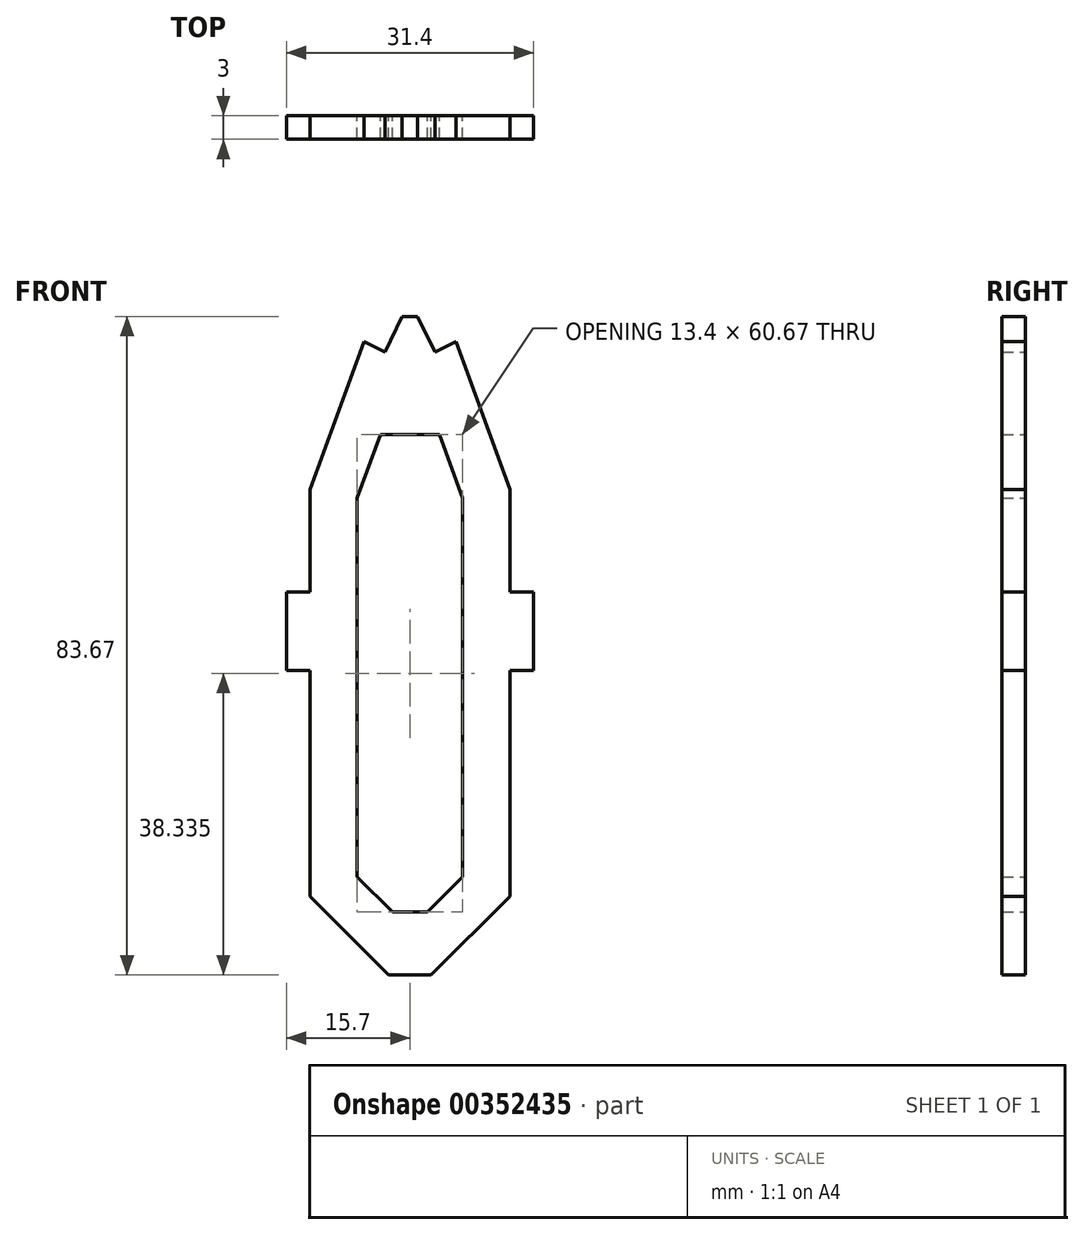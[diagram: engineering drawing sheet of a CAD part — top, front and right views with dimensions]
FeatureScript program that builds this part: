
annotation { "Feature Type Name" : "Feature", "Feature Type Description" : "" }
export const myFeature = defineFeature(function(context is Context, id is Id, definition is map)
    precondition{}
    {
        {
            var Q0;
            Q0=qCreatedBy(makeId("Front.planeOp"),FACE);
            var sketch = newSketch(context, id + "F0", { "sketchPlane" : qUnion([Q0])});
            skLineSegment(sketch, "E0.MirrorCS", {"start": v(5.86, 36.8) * mm, "end": v(3.16, 35.5) * mm});
            skLineSegment(sketch, "E1.MirrorCS", {"start": v(3.16, 35.5) * mm, "end": v(0.99, 40) * mm});
            skLineSegment(sketch, "E2.MirrorCS", {"start": v(12.7, 18) * mm, "end": v(5.86, 36.8) * mm});
            skLineSegment(sketch, "E3.MirrorCS", {"start": v(12.7, -33.67) * mm, "end": v(12.7, -5) * mm});
            skLineSegment(sketch, "E4.bottom", {"start": v(15.7, 5) * mm, "end": v(12.7, 5) * mm});
            skLineSegment(sketch, "E4.top", {"start": v(15.7, -5) * mm, "end": v(12.7, -5) * mm});
            skLineSegment(sketch, "E4.left", {"start": v(15.7, 5) * mm, "end": v(15.7, -5) * mm});
            skLineSegment(sketch, "E5.trimOffspring", {"start": v(12.7, 5) * mm, "end": v(12.7, 18) * mm});
            skLineSegment(sketch, "E6.MirrorCS", {"start": v(-15.7, 5) * mm, "end": v(-12.7, 5) * mm});
            skLineSegment(sketch, "E7.MirrorCS", {"start": v(-15.7, 5) * mm, "end": v(-15.7, -5) * mm});
            skLineSegment(sketch, "E8.MirrorCS", {"start": v(-15.7, -5) * mm, "end": v(-12.7, -5) * mm});
            skLineSegment(sketch, "E9", {"start": v(2.7, -43.67) * mm, "end": v(12.7, -33.67) * mm});
            skLineSegment(sketch, "E10.MirrorCS", {"start": v(-2.7, -43.67) * mm, "end": v(-12.7, -33.67) * mm});
            skLineSegment(sketch, "E11", {"start": v(2.7, -43.67) * mm, "end": v(0, -43.67) * mm});
            skLineSegment(sketch, "E12.MirrorCS", {"start": v(-2.7, -43.67) * mm, "end": v(0, -43.67) * mm});
            skLineSegment(sketch, "E13.MirrorCS", {"start": v(-12.7, -33.67) * mm, "end": v(-12.7, -5) * mm});
            skLineSegment(sketch, "E14", {"start": v(0.99, 40) * mm, "end": v(0, 40) * mm});
            skLineSegment(sketch, "E15.MirrorCS", {"start": v(-0.99, 40) * mm, "end": v(0, 40) * mm});
            skLineSegment(sketch, "E16.MirrorCS", {"start": v(-3.16, 35.5) * mm, "end": v(-0.99, 40) * mm});
            skLineSegment(sketch, "E17.MirrorCS", {"start": v(-5.86, 36.8) * mm, "end": v(-3.16, 35.5) * mm});
            skLineSegment(sketch, "E18.MirrorCS", {"start": v(-12.7, 18) * mm, "end": v(-5.86, 36.8) * mm});
            skLineSegment(sketch, "E19.MirrorCS", {"start": v(-12.7, 5) * mm, "end": v(-12.7, 18) * mm});
            skLineSegment(sketch, "E20", {"start": v(-12.7, 5) * mm, "end": v(-12.7, -5) * mm, "construction": true});
            skLineSegment(sketch, "E21", {"start": v(12.7, 5) * mm, "end": v(12.7, -5) * mm, "construction": true});
            skLineSegment(sketch, "E22.2", {"start": v(2.21, -35.67) * mm, "end": v(6.7, -31.18) * mm});
            skLineSegment(sketch, "E22.3", {"start": v(6.7, -31.18) * mm, "end": v(6.7, -4.52) * mm});
            skLineSegment(sketch, "E22.4", {"start": v(6.7, 5.48) * mm, "end": v(6.7, -4.52) * mm});
            skLineSegment(sketch, "E22.5", {"start": v(-6.7, 16.94) * mm, "end": v(-3.77, 25) * mm});
            skLineSegment(sketch, "E22.6", {"start": v(-6.7, 5) * mm, "end": v(-6.7, 16.94) * mm});
            skLineSegment(sketch, "E22.7", {"start": v(-6.7, 5) * mm, "end": v(-6.7, -5) * mm});
            skLineSegment(sketch, "E22.8", {"start": v(-6.7, -31.18) * mm, "end": v(-6.7, -5) * mm});
            skLineSegment(sketch, "E22.13", {"start": v(6.7, 16.94) * mm, "end": v(3.77, 25) * mm});
            skLineSegment(sketch, "E22.14", {"start": v(-2.21, -35.67) * mm, "end": v(-6.7, -31.18) * mm});
            skLineSegment(sketch, "E22.15", {"start": v(6.7, 5.48) * mm, "end": v(6.7, 16.94) * mm});
            skLineSegment(sketch, "E23", {"start": v(-3.77, 25) * mm, "end": v(3.77, 25) * mm});
            skLineSegment(sketch, "E24", {"start": v(-2.21, -35.67) * mm, "end": v(2.21, -35.67) * mm});
            skSolve(sketch);
        }
        {
            var Q0;
            Q0=makeQuery(id+"F0.imprint","IMPRINT",FACE,{"disambiguationData":[TD([[makeQuery(id+"F0.imprint","IMPRINT",EDGE,{"derivedFrom":sQuery(id+"F0.wireOp",EDGE,"E0.MirrorCS")}),1.0]])]});
            extrude(context, id + "F1", {"entities" : qUnion([Q0]), "depth" : 3 * mm, "symmetric" : true});
        }
    });
